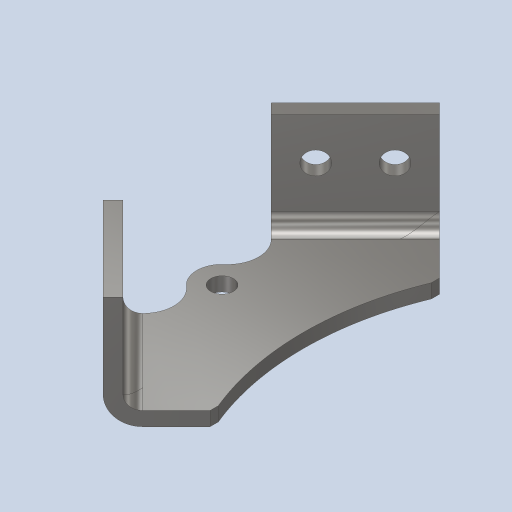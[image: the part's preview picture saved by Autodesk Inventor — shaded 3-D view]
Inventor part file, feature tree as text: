
AUTODESK INVENTOR PART (.ipt)
format: ipt  version: 2023.4 (Build 274418000, 418)  size: 300,544 bytes
history: native  units: in
note: dims shown in document units (in); Inventor stores cm internally (conversion verified against a paired STEP export)
features: projected_geometry x7, sketch x6, sheet_metal_op x5, extrude x3, hole x3, other x2
ambient origin geometry x8: Origin, YZ Plane, XZ Plane, XY Plane, X Axis, Y Axis, Z Axis, Center Point
bodies: Solid1 (feature_tree)
feature tree (26):
  extrude  "Extrusion1"  Depth=3.0in
  sheet_metal_op  "Flange1"
  hole  "Hole1"  [1 undecoded]
  hole  "Hole2"  [1 undecoded]
  hole  "Hole3"  [1 undecoded]
  sheet_metal_op  "Unfold1"
  sketch  "Sketch6"  dims[d13=0.5in d14=0.125in d15=0.125in d16=0.5in d17=0.201in d18=0.75in d19=0.385in d20=0.25in d21=0.5635in d22=0.125in d23=0.8108in d24=0.5in d25=0.201in d26=0.75in d27=0.375in d28=0.25in d29=0.5635in d30=1.0in d31=0.8108in d32=0.201in d33=0.75in d34=0.375in d35=0.25in d36=0.5635in d37=1.0in d38=0.8108in d39=0.311in d40=0.4375in d41=1.0in d42=0.0in d43=5.0in d45=0.5in d46=2.8125in d47=0.2827in d51=0.125in d52=0.0in d53=0.0in]
  extrude  "Extrusion2"  Depth=1.0in TaperAngle=90.0deg
  extrude  "Extrusion3"  Depth=0.125in
  sheet_metal_op  "Refold1"
  sketch  "Sketch1"  dims[d0=0.75in d1=3.0in]
  sketch  "Sketch2"  dims[d2=0.125in d3=0.0in d4=45.0deg]
  other  "Plate1"
  sheet_metal_op  "Bend1"
  sheet_metal_op  "Corner1"
  sketch  "Sketch3"  dims[d5=0.125in d6=0.125in]
  sketch  "Sketch4"  dims[d7=0.0625in d8=0.25in]
  sketch  "Sketch5"  dims[d9=0.125in d10=1.0in d11=90.0deg d12=0.125in]
  projected_geometry  "Projected Loop1"
  projected_geometry  "Projected Loop2"
  projected_geometry  "Projected Loop3"
  projected_geometry  "Projected Loop4"
  projected_geometry  "Project Cut Edges1"
  other  "Definition1"
  projected_geometry  "Project Cut Edges2"
  projected_geometry  "Project Cut Edges3"
note: 3 required parameter values undecoded (feature->parameter linkage not recoverable at this tier; creation-order binding heuristic only, values carry confidence <= 0.55)
